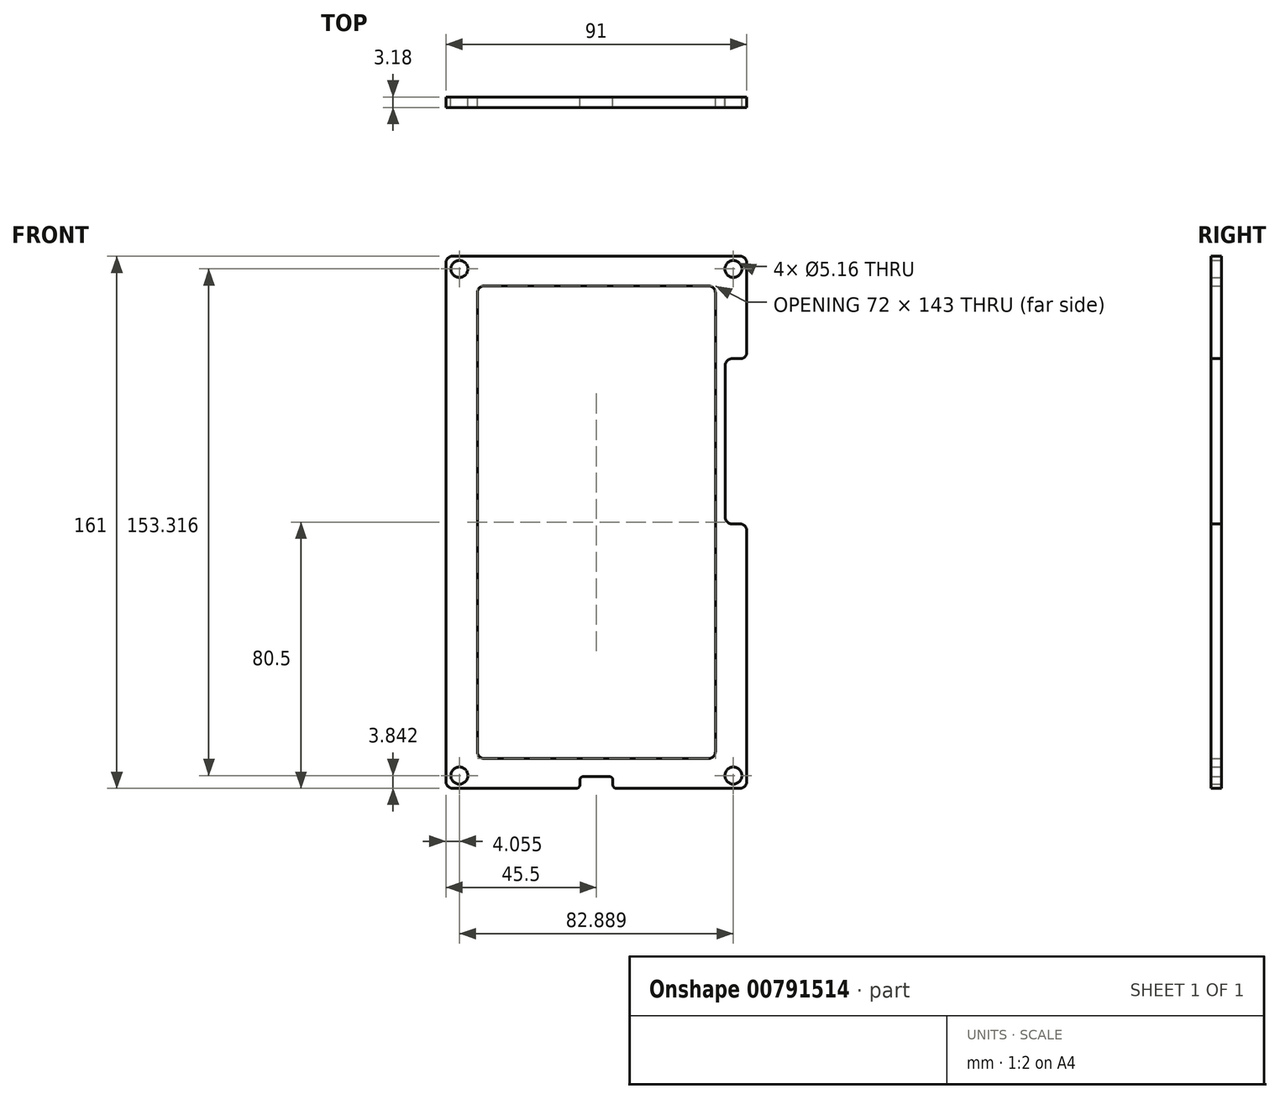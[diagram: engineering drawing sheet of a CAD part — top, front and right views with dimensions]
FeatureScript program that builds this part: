
annotation { "Feature Type Name" : "Feature", "Feature Type Description" : "" }
export const myFeature = defineFeature(function(context is Context, id is Id, definition is map)
    precondition{}
    {
        {
            var Q0;
            Q0=qCreatedBy(makeId("Front.planeOp"),FACE);
            var sketch = newSketch(context, id + "F0", { "sketchPlane" : qUnion([Q0])});
            skLineSegment(sketch, "E0.bottom", {"start": v(39, 74.5) * mm, "end": v(-39, 74.5) * mm});
            skLineSegment(sketch, "E0.top", {"start": v(39, -74.5) * mm, "end": v(-39, -74.5) * mm});
            skLineSegment(sketch, "E0.left", {"start": v(39, 74.5) * mm, "end": v(39, -74.5) * mm});
            skLineSegment(sketch, "E0.right", {"start": v(-39, 74.5) * mm, "end": v(-39, -74.5) * mm});
            skPoint(sketch, "E0.middle", {"position": v(0, 0) * mm});
            skSolve(sketch);
        }
        {
            var Q0;
            Q0=qCreatedBy(makeId("Front.planeOp"),FACE);
            var sketch = newSketch(context, id + "F1", { "sketchPlane" : qUnion([Q0])});
            skLineSegment(sketch, "E1.bottom", {"start": v(36, 71.5) * mm, "end": v(-36, 71.5) * mm});
            skLineSegment(sketch, "E1.top", {"start": v(36, -71.5) * mm, "end": v(-36, -71.5) * mm});
            skLineSegment(sketch, "E1.left", {"start": v(36, 71.5) * mm, "end": v(36, -71.5) * mm});
            skLineSegment(sketch, "E1.right", {"start": v(-36, 71.5) * mm, "end": v(-36, -71.5) * mm});
            skPoint(sketch, "E1.middle", {"position": v(0, 0) * mm});
            skLineSegment(sketch, "E2.bottom", {"start": v(45.5, 80.5) * mm, "end": v(-45.5, 80.5) * mm});
            skLineSegment(sketch, "E2.top", {"start": v(45.5, -80.5) * mm, "end": v(5, -80.5) * mm});
            skLineSegment(sketch, "E2.left", {"start": v(45.5, 80.5) * mm, "end": v(45.5, 49.5) * mm});
            skLineSegment(sketch, "E2.right", {"start": v(-45.5, 80.5) * mm, "end": v(-45.5, -80.5) * mm});
            skLineSegment(sketch, "E3", {"start": v(36, 71.5) * mm, "end": v(45.5, 80.5) * mm, "construction": true});
            skLineSegment(sketch, "E4", {"start": v(-36, 71.5) * mm, "end": v(-45.5, 80.5) * mm, "construction": true});
            skLineSegment(sketch, "E5", {"start": v(36, -71.5) * mm, "end": v(45.5, -80.5) * mm, "construction": true});
            skLineSegment(sketch, "E6", {"start": v(-36, -71.5) * mm, "end": v(-45.5, -80.5) * mm, "construction": true});
            skCircle(sketch, "E7", {"center": v(-41.44, 76.66) * mm, "radius": 2.58 * mm});
            skCircle(sketch, "E8", {"center": v(41.44, 76.66) * mm, "radius": 2.58 * mm});
            skCircle(sketch, "E9", {"center": v(41.44, -76.66) * mm, "radius": 2.58 * mm});
            skCircle(sketch, "E10", {"center": v(-41.44, -76.66) * mm, "radius": 2.58 * mm});
            skLineSegment(sketch, "E11.bottom", {"start": v(45.5, 49.5) * mm, "end": v(39, 49.5) * mm});
            skLineSegment(sketch, "E11.top", {"start": v(45.5, -0.5) * mm, "end": v(39, -0.5) * mm});
            skLineSegment(sketch, "E11.right", {"start": v(39, 49.5) * mm, "end": v(39, -0.5) * mm});
            skLineSegment(sketch, "E12.trimOffspring", {"start": v(45.5, -0.5) * mm, "end": v(45.5, -80.5) * mm});
            skLineSegment(sketch, "E13.top", {"start": v(-5, -77) * mm, "end": v(5, -77) * mm});
            skLineSegment(sketch, "E13.left", {"start": v(-5, -80.5) * mm, "end": v(-5, -77) * mm});
            skLineSegment(sketch, "E13.right", {"start": v(5, -80.5) * mm, "end": v(5, -77) * mm});
            skLineSegment(sketch, "E14", {"start": v(0, 0) * mm, "end": v(0, -100.8) * mm, "construction": true});
            skLineSegment(sketch, "E15.trimOffspring", {"start": v(-5, -80.5) * mm, "end": v(-45.5, -80.5) * mm});
            skSolve(sketch);
        }
        {
            var Q0;
            Q0 = qSketchRegion(id + "F1", true);
            extrude(context, id + "F2", {"entities" : qUnion([Q0]), "depth" : 3.17 * mm, "offsetDistance" : 25 * mm});
        }
        {
            var Q0;
            Q0=makeQuery(id+"F2.opExtrude","SWEPT_EDGE",EDGE,{"disambiguationData":[OSD([sQuery(id+"F1.wireOp",EDGE,"E1.bottom"),sQuery(id+"F1.wireOp",EDGE,"E1.right")])]});
            var Q1;
            Q1=makeQuery(id+"F2.opExtrude","SWEPT_EDGE",EDGE,{"disambiguationData":[OSD([sQuery(id+"F1.wireOp",EDGE,"E1.bottom"),sQuery(id+"F1.wireOp",EDGE,"E1.left")])]});
            var Q2;
            Q2=makeQuery(id+"F2.opExtrude","SWEPT_EDGE",EDGE,{"disambiguationData":[OSD([sQuery(id+"F1.wireOp",EDGE,"E2.bottom"),sQuery(id+"F1.wireOp",EDGE,"E2.right")])]});
            var Q3;
            Q3=makeQuery(id+"F2.opExtrude","SWEPT_EDGE",EDGE,{"disambiguationData":[OSD([sQuery(id+"F1.wireOp",EDGE,"E2.bottom"),sQuery(id+"F1.wireOp",EDGE,"E2.left")])]});
            var Q4;
            Q4=makeQuery(id+"F2.opExtrude","SWEPT_EDGE",EDGE,{"disambiguationData":[OSD([sQuery(id+"F1.wireOp",EDGE,"E2.left"),sQuery(id+"F1.wireOp",EDGE,"E11.bottom")])]});
            var Q5;
            Q5=makeQuery(id+"F2.opExtrude","SWEPT_EDGE",EDGE,{"disambiguationData":[OSD([sQuery(id+"F1.wireOp",EDGE,"E11.bottom"),sQuery(id+"F1.wireOp",EDGE,"E11.right")])]});
            var Q6;
            Q6=makeQuery(id+"F2.opExtrude","SWEPT_EDGE",EDGE,{"disambiguationData":[OSD([sQuery(id+"F1.wireOp",EDGE,"E11.top"),sQuery(id+"F1.wireOp",EDGE,"E12.trimOffspring")])]});
            var Q7;
            Q7=makeQuery(id+"F2.opExtrude","SWEPT_EDGE",EDGE,{"disambiguationData":[OSD([sQuery(id+"F1.wireOp",EDGE,"E11.top"),sQuery(id+"F1.wireOp",EDGE,"E11.right")])]});
            var Q8;
            Q8=makeQuery(id+"F2.opExtrude","SWEPT_EDGE",EDGE,{"disambiguationData":[OSD([sQuery(id+"F1.wireOp",EDGE,"E1.top"),sQuery(id+"F1.wireOp",EDGE,"E1.right")])]});
            var Q9;
            Q9=makeQuery(id+"F2.opExtrude","SWEPT_EDGE",EDGE,{"disambiguationData":[OSD([sQuery(id+"F1.wireOp",EDGE,"E2.right"),sQuery(id+"F1.wireOp",EDGE,"E15.trimOffspring")])]});
            var Q10;
            Q10=makeQuery(id+"F2.opExtrude","SWEPT_EDGE",EDGE,{"disambiguationData":[OSD([sQuery(id+"F1.wireOp",EDGE,"E2.top"),sQuery(id+"F1.wireOp",EDGE,"E12.trimOffspring")])]});
            var Q11;
            Q11=makeQuery(id+"F2.opExtrude","SWEPT_EDGE",EDGE,{"disambiguationData":[OSD([sQuery(id+"F1.wireOp",EDGE,"E1.top"),sQuery(id+"F1.wireOp",EDGE,"E1.left")])]});
            fillet(context, id + "F3", {"entities" : qUnion([Q0, Q1, Q2, Q3, Q4, Q5, Q6, Q7, Q8, Q9, Q10, Q11]), "radius" : 2 * mm, "tangentPropagation" : true, "allowEdgeOverflow" : false});
        }
        {
            var Q0;
            Q0=makeQuery(id+"F2.opExtrude","SWEPT_EDGE",EDGE,{"disambiguationData":[OSD([sQuery(id+"F1.wireOp",EDGE,"E2.top"),sQuery(id+"F1.wireOp",EDGE,"E13.right")])]});
            var Q1;
            Q1=makeQuery(id+"F2.opExtrude","SWEPT_EDGE",EDGE,{"disambiguationData":[OSD([sQuery(id+"F1.wireOp",EDGE,"E13.top"),sQuery(id+"F1.wireOp",EDGE,"E13.right")])]});
            var Q2;
            Q2=makeQuery(id+"F2.opExtrude","SWEPT_EDGE",EDGE,{"disambiguationData":[OSD([sQuery(id+"F1.wireOp",EDGE,"E13.top"),sQuery(id+"F1.wireOp",EDGE,"E13.left")])]});
            var Q3;
            Q3=makeQuery(id+"F2.opExtrude","SWEPT_EDGE",EDGE,{"disambiguationData":[OSD([sQuery(id+"F1.wireOp",EDGE,"E13.left"),sQuery(id+"F1.wireOp",EDGE,"E15.trimOffspring")])]});
            fillet(context, id + "F4", {"entities" : qUnion([Q0, Q1, Q2, Q3]), "radius" : 1 * mm, "tangentPropagation" : true, "allowEdgeOverflow" : false});
        }
    });
